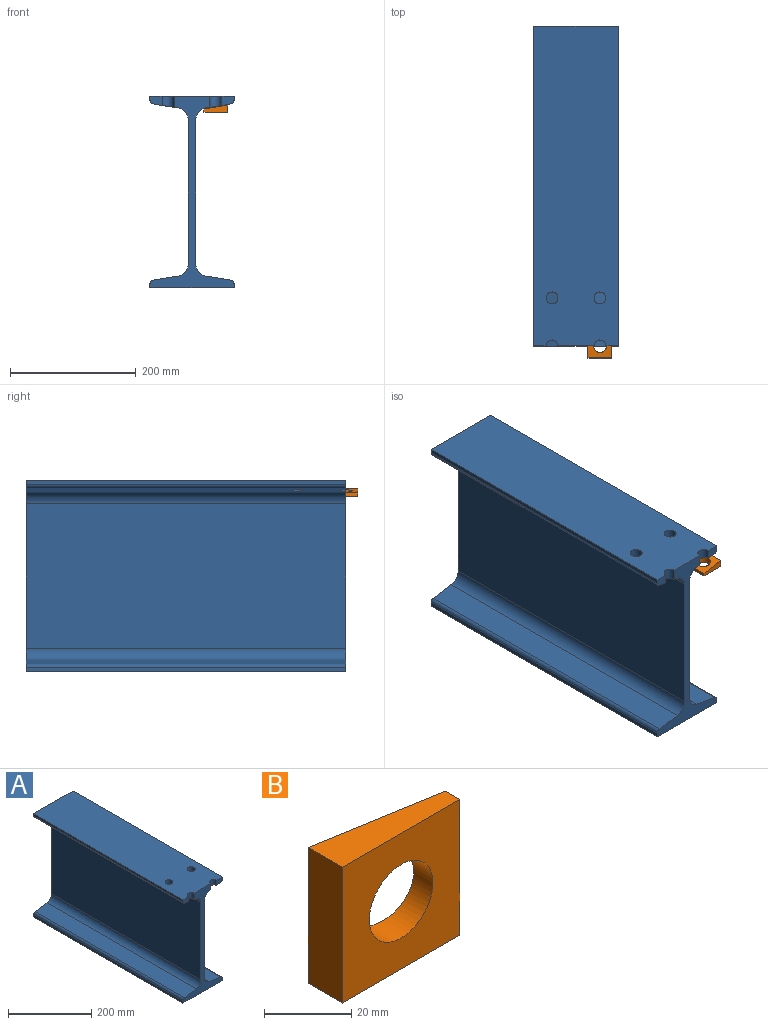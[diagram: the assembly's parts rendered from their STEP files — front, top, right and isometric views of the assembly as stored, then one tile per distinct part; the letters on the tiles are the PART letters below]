
ASSEMBLY  parts=2 mates=1
PART A: 28 faces, bbox 133.4x508x304.8 mm
  f0: plane 508x133.4mm, normal (0,0,1), area 66912.5mm2, adj f1,f2,f3,f17,f18,f23,f24,f25
  f1: plane 304.8x133.4mm, normal (0,-1,0), area 6714.5mm2, adj f0,f4,f5,f6,f7,f8,f9,f10
  f2: plane 19.08x14.92mm, normal (0,-1,0), area 250.4mm2, adj f0,f18,f19,f20,f25
  f3: plane 19.08x14.92mm, normal (0,-1,0), area 250.4mm2, adj f0,f15,f16,f17,f24
  f4: cylinder r=19.05mm len=508mm, axis (0,1,0), area 13665.9mm2, adj f1,f5,f22,f23
  f5: plane 508x39.79mm, normal (-0.16,0,0.99), area 20472.8mm2, adj f1,f4,f6,f23
  f6: cylinder r=5.94mm len=508mm, axis (0,1,0), area 4258.3mm2, adj f1,f5,f7,f23
  f7: plane 508x6.81mm, normal (-1,0,0), area 3459.6mm2, adj f1,f6,f8,f23
  f8: plane 508x133.4mm, normal (0,0,-1), area 67767.6mm2, adj f1,f7,f9,f23
  f9: plane 508x6.81mm, normal (1,0,0), area 3459.6mm2, adj f1,f8,f10,f23
  f10: cylinder r=5.94mm len=508mm, axis (0,1,0), area 4258.3mm2, adj f1,f9,f11,f23
  f11: plane 508x39.79mm, normal (0.16,0,0.99), area 20472.8mm2, adj f1,f10,f12,f23
  f12: cylinder r=19.05mm len=508mm, axis (0,1,0), area 13665.8mm2, adj f1,f11,f13,f23
  f13: plane 508x229.1mm, normal (1,0,0), area 116383.3mm2, adj f1,f12,f14,f23
  f14: cylinder r=19.05mm len=508mm, axis (0,1,0), area 13665.9mm2, adj f1,f13,f15,f23
  f15: plane 508x39.79mm, normal (0.16,0,-0.99), area 20039.8mm2, adj f1,f3,f14,f16,f23,f24,f27
  f16: cylinder r=5.94mm len=508mm, axis (0,1,0), area 4258.3mm2, adj f3,f15,f17,f23
  f17: plane 508x6.81mm, normal (1,0,0), area 3459.6mm2, adj f0,f3,f16,f23
  f18: plane 508x6.81mm, normal (-1,0,0), area 3459.6mm2, adj f0,f2,f19,f23
  f19: cylinder r=5.94mm len=508mm, axis (0,1,0), area 4258.3mm2, adj f2,f18,f20,f23
  f20: plane 508x39.79mm, normal (-0.16,0,-0.99), area 20039.8mm2, adj f1,f2,f19,f21,f23,f25,f26
  f21: cylinder r=19.05mm len=508mm, axis (0,1,0), area 13665.9mm2, adj f1,f20,f22,f23
  f22: plane 508x229.1mm, normal (-1,0,0), area 116383.3mm2, adj f1,f4,f21,f23
  f23: plane 304.8x133.4mm, normal (0,1,0), area 7842mm2, adj f0,f4,f5,f6,f7,f8,f9,f10
  f24: cylinder r=9.53mm len=19.05mm, axis (0,0,1), area 492.2mm2, adj f0,f1,f3,f15
  f25: cylinder r=9.53mm len=19.05mm, axis (0,0,1), area 492.2mm2, adj f0,f1,f2,f20
  f26: cylinder r=9.53mm len=19.05mm, axis (0,0,1), area 984.4mm2, adj f0,f20
  f27: cylinder r=9.53mm len=19.05mm, axis (0,0,1), area 984.4mm2, adj f0,f15
PART B: 7 faces, bbox 38.1x11.1x38.1 mm
  f0: plane 38.1x4.78mm, normal (1,0,0), area 181.9mm2, adj f1,f3,f4,f5
  f1: plane 38.1x38.1mm, normal (0.16,0.99,0), area 1132.9mm2, adj f0,f2,f4,f5,f6
  f2: plane 38.1x11.13mm, normal (-1,0,0), area 423.9mm2, adj f1,f3,f4,f5
  f3: plane 38.1x38.1mm, normal (0,-1,0), area 1117.5mm2, adj f0,f2,f4,f5,f6
  f4: plane 38.1x11.13mm, normal (0,0,1), area 302.9mm2, adj f0,f1,f2,f3
  f5: plane 38.1x11.13mm, normal (0,0,-1), area 302.9mm2, adj f0,f1,f2,f3
  f6: cylinder r=10.31mm len=20.62mm, axis (0,-1,0), area 515.1mm2, adj f1,f3
PLACE A at identity fixed
PLACE B rot(axis=(0,0.71,0.71),180deg) t=(-1030.68,-533.4,494.21)mm
MATE fastened B.f6 <-> A.f24  axis (0,0,-1) through (-1030.68,-533.4,494.21)mm
